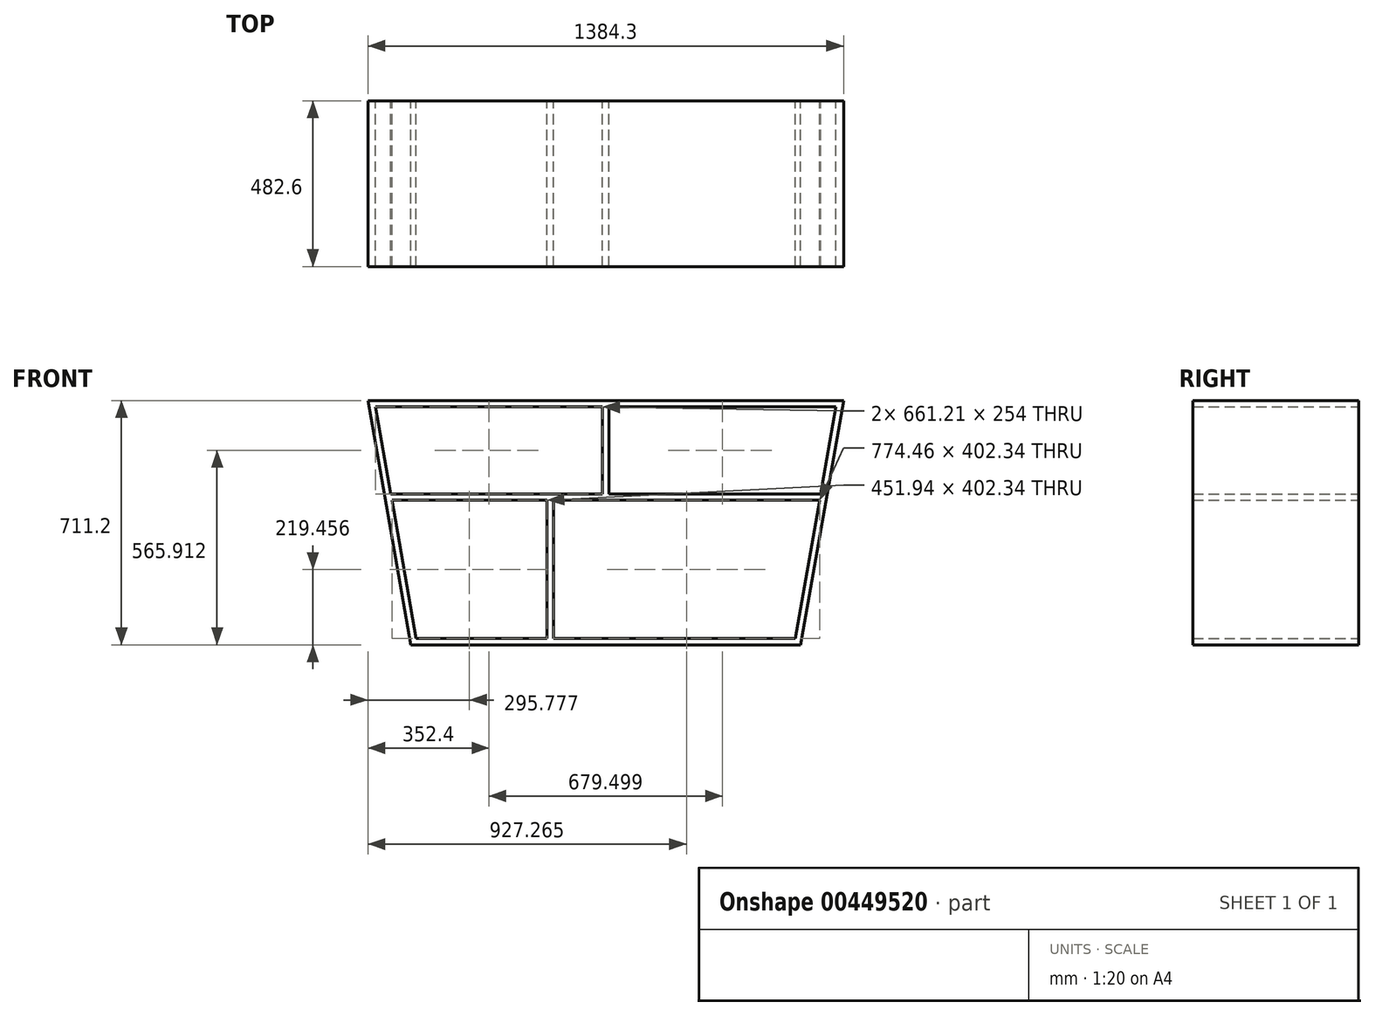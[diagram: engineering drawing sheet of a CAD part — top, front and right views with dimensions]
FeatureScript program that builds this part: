
annotation { "Feature Type Name" : "Feature", "Feature Type Description" : "" }
export const myFeature = defineFeature(function(context is Context, id is Id, definition is map)
    precondition{}
    {
        {
            var Q0;
            Q0=qCreatedBy(makeId("Front.planeOp"),FACE);
            var sketch = newSketch(context, id + "F0", { "sketchPlane" : qUnion([Q0])});
            skLineSegment(sketch, "E0", {"start": v(-1043.18, 0) * mm, "end": v(90.32, 0) * mm});
            skLineSegment(sketch, "E1", {"start": v(90.32, 0) * mm, "end": v(215.72, 711.2) * mm});
            skLineSegment(sketch, "E2", {"start": v(215.72, 711.2) * mm, "end": v(-1168.58, 711.2) * mm});
            skLineSegment(sketch, "E3", {"start": v(-1168.58, 711.2) * mm, "end": v(-1043.18, 0) * mm});
            skLineSegment(sketch, "E4.0", {"start": v(193.92, 692.91) * mm, "end": v(-467.29, 692.91) * mm});
            skLineSegment(sketch, "E4.1", {"start": v(74.97, 18.29) * mm, "end": v(145.91, 420.62) * mm});
            skLineSegment(sketch, "E4.2", {"start": v(-1027.83, 18.29) * mm, "end": v(-646.83, 18.29) * mm});
            skLineSegment(sketch, "E4.3", {"start": v(-1146.79, 692.91) * mm, "end": v(-1102, 438.91) * mm});
            skLineSegment(sketch, "E5", {"start": v(-1102, 438.91) * mm, "end": v(-485.57, 438.91) * mm});
            skLineSegment(sketch, "E6", {"start": v(-1098.77, 420.62) * mm, "end": v(-646.83, 420.62) * mm});
            skLineSegment(sketch, "E7.trimOffspring", {"start": v(-1098.77, 420.62) * mm, "end": v(-1027.83, 18.29) * mm});
            skLineSegment(sketch, "E8.trimOffspring", {"start": v(149.14, 438.91) * mm, "end": v(193.92, 692.91) * mm});
            skLineSegment(sketch, "E9", {"start": v(-646.83, 420.62) * mm, "end": v(-646.83, 18.29) * mm});
            skLineSegment(sketch, "E10", {"start": v(-628.54, 18.29) * mm, "end": v(-628.54, 420.62) * mm});
            skLineSegment(sketch, "E11.trimOffspring", {"start": v(-628.54, 420.62) * mm, "end": v(145.91, 420.62) * mm});
            skLineSegment(sketch, "E12.trimOffspring", {"start": v(-628.54, 18.29) * mm, "end": v(74.97, 18.29) * mm});
            skLineSegment(sketch, "E13", {"start": v(-485.57, 692.91) * mm, "end": v(-485.57, 438.91) * mm});
            skLineSegment(sketch, "E14", {"start": v(-467.29, 692.91) * mm, "end": v(-467.29, 438.91) * mm});
            skLineSegment(sketch, "E15", {"start": v(-476.43, 692.91) * mm, "end": v(-476.43, 438.91) * mm, "construction": true});
            skLineSegment(sketch, "E16.trimOffspring", {"start": v(-485.57, 692.91) * mm, "end": v(-1146.79, 692.91) * mm});
            skLineSegment(sketch, "E17.trimOffspring", {"start": v(-467.29, 438.91) * mm, "end": v(149.14, 438.91) * mm});
            skLineSegment(sketch, "E18", {"start": v(-1146.79, 692.91) * mm, "end": v(-1165.36, 692.91) * mm, "construction": true});
            skLineSegment(sketch, "E19", {"start": v(-1146.79, 692.91) * mm, "end": v(-1150.01, 711.2) * mm, "construction": true});
            skLineSegment(sketch, "E20", {"start": v(-1102, 438.91) * mm, "end": v(-1098.77, 420.62) * mm, "construction": true});
            skLineSegment(sketch, "E21", {"start": v(-1027.83, 18.29) * mm, "end": v(-1046.4, 18.29) * mm, "construction": true});
            skLineSegment(sketch, "E22", {"start": v(74.97, 18.29) * mm, "end": v(93.54, 18.29) * mm, "construction": true});
            skLineSegment(sketch, "E23", {"start": v(193.92, 692.91) * mm, "end": v(212.5, 692.91) * mm, "construction": true});
            skSolve(sketch);
        }
        {
            var Q0;
            Q0=makeQuery(id+"F0.imprint","IMPRINT",FACE,{"disambiguationData":[TD([[makeQuery(id+"F0.imprint","IMPRINT",EDGE,{"derivedFrom":sQuery(id+"F0.wireOp",EDGE,"E0")}),1.0]])]});
            extrude(context, id + "F1", {"entities" : qUnion([Q0]), "depth" : 482.6 * mm});
        }
    });
